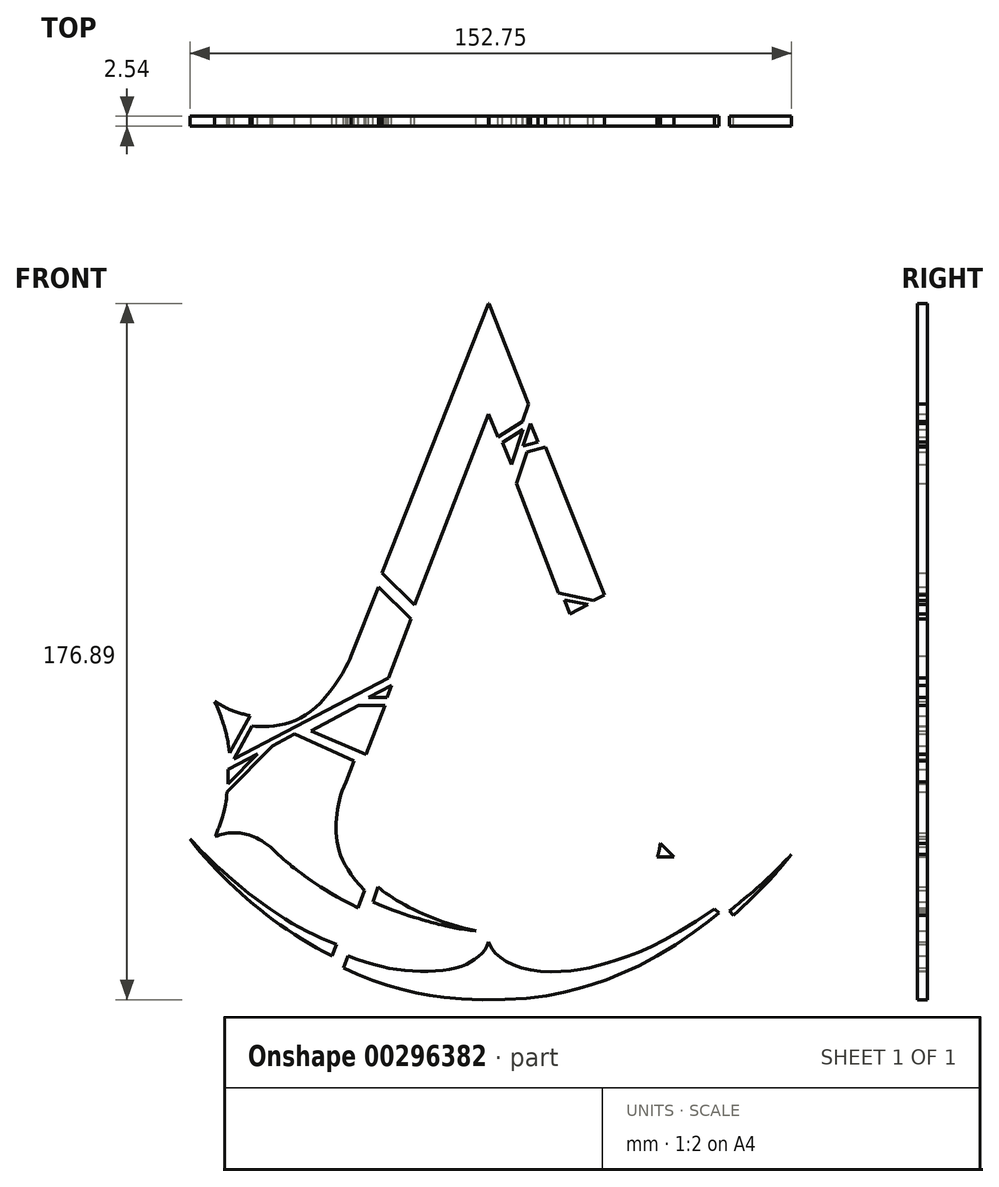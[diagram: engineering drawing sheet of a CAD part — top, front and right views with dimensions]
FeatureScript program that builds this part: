
annotation { "Feature Type Name" : "Feature", "Feature Type Description" : "" }
export const myFeature = defineFeature(function(context is Context, id is Id, definition is map)
    precondition{}
    {
        {
            var Q0;
            Q0=qCreatedBy(makeId("Front.planeOp"),FACE);
            var sketch = newSketch(context, id + "F0", { "sketchPlane" : qUnion([Q0])});
            skLineSegment(sketch, "E0", {"start": v(-27.45, 15.41) * mm, "end": v(-0.43, 83.86) * mm});
            skLineSegment(sketch, "E1", {"start": v(-0.43, 83.86) * mm, "end": v(-0.3, 83.86) * mm});
            skLineSegment(sketch, "E2", {"start": v(-0.3, 83.86) * mm, "end": v(9.77, 58.3) * mm});
            skLineSegment(sketch, "E3", {"start": v(9.77, 58.3) * mm, "end": v(8.28, 53.85) * mm});
            skLineSegment(sketch, "E4", {"start": v(8.28, 53.85) * mm, "end": v(2.03, 49.88) * mm});
            skLineSegment(sketch, "E5", {"start": v(2.03, 49.88) * mm, "end": v(-0.33, 55.74) * mm});
            skLineSegment(sketch, "E6", {"start": v(-0.33, 55.74) * mm, "end": v(-19.16, 7.3) * mm});
            skLineSegment(sketch, "E7", {"start": v(-19.16, 7.3) * mm, "end": v(-27.45, 15.41) * mm});
            skLineSegment(sketch, "E8", {"start": v(8.35, 51.83) * mm, "end": v(5.44, 42.98) * mm});
            skLineSegment(sketch, "E9", {"start": v(5.44, 42.98) * mm, "end": v(3.21, 48.58) * mm});
            skLineSegment(sketch, "E10", {"start": v(3.21, 48.58) * mm, "end": v(8.35, 51.83) * mm});
            skLineSegment(sketch, "E11", {"start": v(10.25, 53.35) * mm, "end": v(8.35, 47.59) * mm});
            skLineSegment(sketch, "E12", {"start": v(8.35, 47.59) * mm, "end": v(12.2, 48.6) * mm});
            skLineSegment(sketch, "E13", {"start": v(12.2, 48.6) * mm, "end": v(10.25, 53.35) * mm});
            skLineSegment(sketch, "E14", {"start": v(14.15, 47.39) * mm, "end": v(9.4, 46.13) * mm});
            skLineSegment(sketch, "E15", {"start": v(9.4, 46.13) * mm, "end": v(6.74, 38.07) * mm});
            skLineSegment(sketch, "E16", {"start": v(6.74, 38.07) * mm, "end": v(17.43, 10.35) * mm});
            skLineSegment(sketch, "E17", {"start": v(17.43, 10.35) * mm, "end": v(26.31, 8.44) * mm});
            skLineSegment(sketch, "E18", {"start": v(26.31, 8.44) * mm, "end": v(29.02, 9.8) * mm});
            skLineSegment(sketch, "E19", {"start": v(29.02, 9.8) * mm, "end": v(14.15, 47.39) * mm});
            skLineSegment(sketch, "E20", {"start": v(24.86, 7.38) * mm, "end": v(18.96, 8.57) * mm});
            skLineSegment(sketch, "E21", {"start": v(18.96, 8.57) * mm, "end": v(20.29, 4.94) * mm});
            skLineSegment(sketch, "E22", {"start": v(20.29, 4.94) * mm, "end": v(24.86, 7.38) * mm});
            skLineSegment(sketch, "E23", {"start": v(33.18, 9.28) * mm, "end": v(23.72, 4.3) * mm});
            skLineSegment(sketch, "E24", {"start": v(23.72, 4.3) * mm, "end": v(39.76, -36.96) * mm});
            skFitSpline(sketch, "E25", {"points": [v(39.76, -36.96) * mm, v(42.18, -44.62) * mm, v(42.49, -48.96) * mm], "startDerivative": vector(6.74, -14.2) * mm, "endDerivative": vector(-0.6, -4.59) * mm});
            skLineSegment(sketch, "E26", {"start": v(42.49, -48.96) * mm, "end": v(53.4, -59.54) * mm});
            skLineSegment(sketch, "E27", {"start": v(53.4, -59.54) * mm, "end": v(59.01, -54.34) * mm});
            skFitSpline(sketch, "E28", {"points": [v(59.01, -54.34) * mm, v(64.5, -51.24) * mm, v(68.44, -50.55) * mm, v(73.15, -51.54) * mm], "startDerivative": vector(16.64, 12.64) * mm, "endDerivative": vector(18.8, -6.94) * mm});
            skFitSpline(sketch, "E29", {"points": [v(73.15, -51.54) * mm, v(69.95, -36.86) * mm, v(69.95, -36.86) * mm, v(69.95, -36.86) * mm, v(73.96, -18.09) * mm], "startDerivative": vector(-23.27, 54.6) * mm, "endDerivative": vector(26.52, 52.96) * mm});
            skLineSegment(sketch, "E30", {"start": v(33.18, 9.28) * mm, "end": v(38.2, -3.26) * mm});
            skFitSpline(sketch, "E31", {"points": [v(38.2, -3.26) * mm, v(44.94, -14.3) * mm, v(53.9, -20.84) * mm, v(65.85, -21.45) * mm, v(73.96, -18.09) * mm], "startDerivative": vector(33.94, -75.59) * mm, "endDerivative": vector(38.4, 22.9) * mm});
            skLineSegment(sketch, "E32", {"start": v(-25.08, -13.13) * mm, "end": v(-26.16, -16.27) * mm});
            skLineSegment(sketch, "E33", {"start": v(-26.16, -16.27) * mm, "end": v(-30.89, -16.27) * mm});
            skLineSegment(sketch, "E34", {"start": v(-30.89, -16.27) * mm, "end": v(-25.08, -13.13) * mm});
            skLineSegment(sketch, "E35", {"start": v(-28.3, 11.79) * mm, "end": v(-20.08, 3.74) * mm});
            skLineSegment(sketch, "E36", {"start": v(-20.08, 3.74) * mm, "end": v(-25.84, -11.29) * mm});
            skLineSegment(sketch, "E37", {"start": v(-25.84, -11.29) * mm, "end": v(-65.06, -31.92) * mm});
            skLineSegment(sketch, "E38", {"start": v(-65.06, -31.92) * mm, "end": v(-60.43, -23.48) * mm});
            skLineSegment(sketch, "E39", {"start": v(-28.3, 11.79) * mm, "end": v(-35.26, -5.71) * mm});
            skFitSpline(sketch, "E40", {"points": [v(-35.26, -5.71) * mm, v(-42.54, -17) * mm, v(-52.93, -23.17) * mm, v(-60.43, -23.48) * mm], "startDerivative": vector(-3.79, -12.5) * mm, "endDerivative": vector(-16.58, 2.82) * mm});
            skLineSegment(sketch, "E41", {"start": v(-45.53, -24.75) * mm, "end": v(-31.56, -30.77) * mm});
            skLineSegment(sketch, "E42", {"start": v(-31.56, -30.77) * mm, "end": v(-26.69, -18.28) * mm});
            skLineSegment(sketch, "E43", {"start": v(-26.69, -18.28) * mm, "end": v(-33.46, -18.28) * mm});
            skLineSegment(sketch, "E44", {"start": v(-33.46, -18.28) * mm, "end": v(-45.53, -24.75) * mm});
            skLineSegment(sketch, "E45", {"start": v(-59.02, -30.54) * mm, "end": v(-66.53, -34.48) * mm});
            skLineSegment(sketch, "E46", {"start": v(-66.53, -34.48) * mm, "end": v(-66.53, -38.27) * mm});
            skLineSegment(sketch, "E47", {"start": v(-66.53, -38.27) * mm, "end": v(-59.02, -30.54) * mm});
            skLineSegment(sketch, "E48", {"start": v(-60.9, -20.95) * mm, "end": v(-66.14, -30.33) * mm});
            skFitSpline(sketch, "E49", {"points": [v(-69.95, -17.24) * mm, v(-64.6, -19.88) * mm, v(-60.9, -20.95) * mm], "startDerivative": vector(13.52, -8.5) * mm, "endDerivative": vector(6.43, -1.59) * mm});
            skFitSpline(sketch, "E50", {"points": [v(-69.95, -17.24) * mm, v(-67.3, -24.44) * mm, v(-66.14, -30.33) * mm], "startDerivative": vector(7.18, -14.14) * mm, "endDerivative": vector(3.2, -22.02) * mm});
            skLineSegment(sketch, "E51", {"start": v(-36.62, -37.67) * mm, "end": v(-34.53, -32.31) * mm});
            skLineSegment(sketch, "E52", {"start": v(-34.53, -32.31) * mm, "end": v(-49.73, -25.57) * mm});
            skLineSegment(sketch, "E53", {"start": v(-49.73, -25.57) * mm, "end": v(-55.26, -28.5) * mm});
            skLineSegment(sketch, "E54", {"start": v(-55.26, -28.5) * mm, "end": v(-66.81, -40.27) * mm});
            skFitSpline(sketch, "E55", {"points": [v(-66.81, -40.27) * mm, v(-68.43, -47.93) * mm, v(-69.82, -51.6) * mm], "startDerivative": vector(-1.75, -21.3) * mm, "endDerivative": vector(-4.26, -8.74) * mm});
            skFitSpline(sketch, "E56", {"points": [v(-69.82, -51.6) * mm, v(-63.95, -50.63) * mm, v(-55.73, -54.2) * mm], "startDerivative": vector(12.66, 4.95) * mm, "endDerivative": vector(18.16, -13.05) * mm});
            skFitSpline(sketch, "E57", {"points": [v(-55.73, -54.2) * mm, v(-49.85, -59.5) * mm, v(-33.5, -69.72) * mm], "startDerivative": vector(26.06, -25.86) * mm, "endDerivative": vector(46.15, -23.16) * mm});
            skLineSegment(sketch, "E58", {"start": v(-33.5, -69.72) * mm, "end": v(-31.9, -65.25) * mm});
            skFitSpline(sketch, "E59", {"points": [v(-36.62, -37.67) * mm, v(-39.1, -50.2) * mm, v(-31.9, -65.25) * mm], "startDerivative": vector(-12, -26.1) * mm, "endDerivative": vector(31.26, -32.01) * mm});
            skLineSegment(sketch, "E60", {"start": v(42.46, -56.7) * mm, "end": v(46.73, -56.7) * mm});
            skLineSegment(sketch, "E61", {"start": v(46.73, -56.7) * mm, "end": v(43.24, -53.28) * mm});
            skFitSpline(sketch, "E62", {"points": [v(43.24, -53.28) * mm, v(42.46, -56.7) * mm], "startDerivative": vector(-0.61, -4.88) * mm, "endDerivative": vector(-1.22, -2.44) * mm});
            skLineSegment(sketch, "E63", {"start": v(-28.49, -64.44) * mm, "end": v(-29.7, -68.18) * mm});
            skFitSpline(sketch, "E64", {"points": [v(-28.49, -64.44) * mm, v(-18.78, -70.43) * mm, v(-3.56, -75.54) * mm], "startDerivative": vector(13.68, -11.01) * mm, "endDerivative": vector(23.98, -4.5) * mm});
            skFitSpline(sketch, "E65", {"points": [v(-29.7, -68.18) * mm, v(-16.29, -72.97) * mm, v(-13.34, -73.79) * mm, v(-3.56, -75.54) * mm], "startDerivative": vector(37.54, -17.88) * mm, "endDerivative": vector(33.45, -2.58) * mm});
            skLineSegment(sketch, "E66", {"start": v(41.95, -58.11) * mm, "end": v(48.16, -58.11) * mm});
            skLineSegment(sketch, "E67", {"start": v(48.16, -58.11) * mm, "end": v(52.5, -62.43) * mm});
            skFitSpline(sketch, "E68", {"points": [v(41.95, -58.11) * mm, v(27.12, -73.13) * mm, v(27.12, -73.13) * mm, v(9.3, -79.62) * mm], "startDerivative": vector(-23.1, -59.1) * mm, "endDerivative": vector(-67.74, -15.1) * mm});
            skFitSpline(sketch, "E69", {"points": [v(52.5, -62.43) * mm, v(41.7, -69.31) * mm, v(27.81, -75.28) * mm, v(26.75, -75.6) * mm, v(9.3, -79.62) * mm], "startDerivative": vector(-32.44, -23.95) * mm, "endDerivative": vector(-51.86, -1.3) * mm});
            skFitSpline(sketch, "E70", {"points": [v(60.82, -70.49) * mm, v(68.66, -63.94) * mm, v(76.56, -56.13) * mm], "startDerivative": vector(9.48, 7.61) * mm, "endDerivative": vector(15.72, 16.58) * mm});
            skFitSpline(sketch, "E71", {"points": [v(76.56, -56.13) * mm, v(69.38, -64.4) * mm, v(61.88, -71.58) * mm], "startDerivative": vector(-13.6, -16.7) * mm, "endDerivative": vector(-6.6, -6.59) * mm});
            skLineSegment(sketch, "E72", {"start": v(60.82, -70.49) * mm, "end": v(61.88, -71.58) * mm});
            skLineSegment(sketch, "E73", {"start": v(-39.03, -78.99) * mm, "end": v(-40.17, -81.96) * mm});
            skFitSpline(sketch, "E74", {"points": [v(-39.03, -78.99) * mm, v(-54.32, -71.07) * mm, v(-69.08, -59.37) * mm, v(-76.2, -52.13) * mm], "startDerivative": vector(-42.94, 16.36) * mm, "endDerivative": vector(-17.05, 20.6) * mm});
            skFitSpline(sketch, "E75", {"points": [v(-40.17, -81.96) * mm, v(-55.49, -72.43) * mm, v(-68.33, -61.21) * mm, v(-76.2, -52.13) * mm], "startDerivative": vector(-45.62, 23.16) * mm, "endDerivative": vector(-10.87, 18.17) * mm});
            skLineSegment(sketch, "E76", {"start": v(-36.03, -81.92) * mm, "end": v(-37.17, -84.97) * mm});
            skFitSpline(sketch, "E77", {"points": [v(-37.17, -84.97) * mm, v(-27.47, -88.92) * mm, v(-18.36, -91.36) * mm, v(-8.88, -92.72) * mm, v(10.51, -92.54) * mm, v(23.07, -90.04) * mm, v(31.92, -87.05) * mm, v(47.13, -79.1) * mm, v(58.14, -70.97) * mm], "startDerivative": vector(72.84, -36.33) * mm, "endDerivative": vector(44.51, 35.63) * mm});
            skFitSpline(sketch, "E78", {"points": [v(-36.03, -81.92) * mm, v(-20.37, -85.7) * mm, v(-8.29, -84.84) * mm, v(-3.05, -82.13) * mm, v(-0.36, -78.35) * mm], "startDerivative": vector(50.98, -20.49) * mm, "endDerivative": vector(5.56, 25.41) * mm});
            skFitSpline(sketch, "E79", {"points": [v(-0.36, -78.35) * mm, v(2.63, -82.34) * mm, v(9.87, -85.42) * mm, v(21.7, -85.53) * mm, v(31.71, -83.14) * mm, v(57.06, -69.93) * mm], "startDerivative": vector(19.58, -47.72) * mm, "endDerivative": vector(113.15, 79.99) * mm});
            skLineSegment(sketch, "E80", {"start": v(58.14, -70.97) * mm, "end": v(57.06, -69.93) * mm});
            skSolve(sketch);
        }
        {
            var Q0;
            Q0 = qSketchRegion(id + "F0", true);
            extrude(context, id + "F1", {"entities" : qUnion([Q0]), "depth" : 2.54 * mm});
        }
    });
